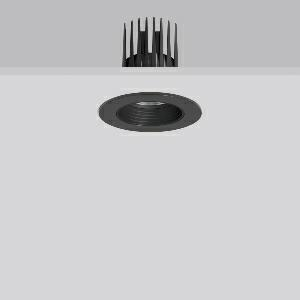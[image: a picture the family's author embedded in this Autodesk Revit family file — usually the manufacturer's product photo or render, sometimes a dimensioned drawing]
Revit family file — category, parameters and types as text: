
# Revit family: heledon_mini_e_901753_003_3_76_ab0e
name_source: partatom
category: Lighting Fixtures
units: mm (PartAtom-declared; Revit-internal decimal feet)

## family parameters
Cut with Voids When Loaded = No
Host = Face
Light Source = No
Part Type = Normal
Room Calculation Point = No
Round Connector Dimension = Use Diameter
Shared = No

## types (1)
- HELEDON mini E (1 x LED Modul 935, 2900 lm, 3500)
    Apparent Load = 29 VA
    Approval mark = CE
    CIE Flux Codes = 98 100 100 100 100
    Color Rendering = 92
    Color Temperature = 3500
    Default Elevation = 1800 mm
    Description = Series: HELEDON mini
Round recessed downlight. Housing: die-cast aluminium, powder-coated. Black plastic ring and recessed LED to prevent glare from the side. Optical assembly with lens made of plastic (polycarbonate) for the best homogeneous light distribution - can be changed without tools. Best colour rendering index Ra>90. Suitable for Recessed ceiling mounting. Installation without tools thanks to spring fastening system. Including separate LED converter with connecting cable 600 mm.High quality converter without flickering and stroboscopic effect. Through-wiring box (5 pole) available as accessory. The following accessories can be mounted without use of tools: interchangeable lenses, decorative glasses, honeycomb louvre, clear and frosted diffusers, white interchangeable plastic ring. 
Colour: deep black, matt (RAL 9005)
Diameter: 124 mm
Height: 3 mm
Cut-out diameter: 114 mm
Recess height: 170 mm
Luminaire: recess height: 120 mm
Lamp: LED
Socket: without socket
Colour temperature: 3500K
Colour rendering index (CRI): 92
System power: 29 W
Rated luminous flux: 2900 lm
Luminous efficiency: 100 lm/W
Control gear: Converter, dimmable, DALI
Protection class: II
Type of protection: IP 20
    Height = 0 mm  [stored 0 ft]
    Lamp = 1 x LED Modul 935
    Lamp Light Flux = 2900 lm
    Lamp count = 1
    Length = 124 mm  [stored 0.406824 ft]
    Lifetime = 50000 h
    Luminous efficacy = 100 lm/W
    Manufacturer = RZB
    ModVariant = No
    Model = 901753.003.3.76
    Mounting Place = Ceiling
    Mounting Type = Recessed
    Number of Poles = 1
    OnlyDefault = Yes
    Power Factor = 1
    Product Name = HELEDON mini E
    Product group = Recessed downlights
    ProductGroupID = 402
    Protection Class = Protection class II
    Protection Degree = IP 20
    RLX_Detail_Level = 1
    RLX_Emergency_Light_Flux = 0 lm
    RLX_Emergency_Type = 0
    RLX_Emergency_Type_DB = No
    RlxData = <blob elided: 126169 chars, md5=219fadc3>
    Socket = socket
    Standby Power = 0 W
    System Light Flux = 2900 lm
    System Power = 29 W
    Type Comments = Product without accessories
    Type Image = 901656.003.jpg
    URL = http://relux.com
    VarID = ---
    Voltage = 230 V
    Voltage Range = 220-240 V
    Weight = 0.00 kg
    Width = 0 mm  [stored 0 ft]

note: [stored X ft] marks values corroborated as IEEE doubles in the binary element streams (Revit-internal decimal feet)

## geometry (parser evidence)
native form markers: Blend x4, Sweep x12
no freeform markers — native parametric forms only
